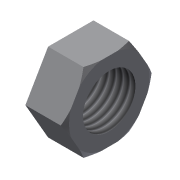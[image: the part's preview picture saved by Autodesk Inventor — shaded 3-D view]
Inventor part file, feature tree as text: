
AUTODESK INVENTOR PART (.ipt)
format: ipt  version: 2022.5 (Build 265521000, 521)  size: 113,664 bytes
history: native  units: in
note: dims shown in document units (in); Inventor stores cm internally (conversion verified against a paired STEP export)
features: sketch x2, revolve x1, chamfer x1, extrude x1, thread x1
ambient origin geometry x8: Origin, YZ Plane, XZ Plane, XY Plane, X Axis, Y Axis, Z Axis, Center Point
bodies: Solid1 (feature_tree)
feature tree (6):
  revolve  "Revolution3"  [1 undecoded]
  chamfer  "Chamfer2"  Distance=0.0866in
  extrude  "Extrusion15"  TaperAngle=90.0deg  [1 undecoded]
  thread  "Thread2"  [1 undecoded]
  sketch  "Sketch17"  dims[d96=0.0591in d98=0.1024in]
  sketch  "Sketch18"  dims[d99=0.0in d100=0.0866in d102=90.0deg d103=0.0118in d104=0.0787in d105=30.0deg d106=0.1024in d107=0.3937in d108=0.0in d109=0.3937in d110=0.0in]
note: 3 required parameter values undecoded (feature->parameter linkage not recoverable at this tier; creation-order binding heuristic only, values carry confidence <= 0.55)